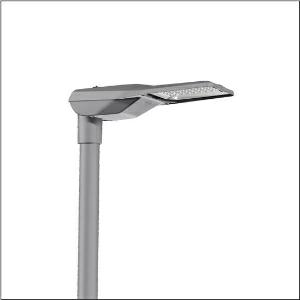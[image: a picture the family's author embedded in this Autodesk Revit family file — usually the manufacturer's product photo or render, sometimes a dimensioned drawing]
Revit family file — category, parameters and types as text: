
# Revit family: streetlight_sl_21_iq_mini___st1_0ab_5xe2m31v08jb_8772
name_source: partatom
category: Lighting Fixtures
units: mm (PartAtom-declared; Revit-internal decimal feet)

## family parameters
Cut with Voids When Loaded = No
Host = Face
Light Source = No
Part Type = Normal
Room Calculation Point = No
Round Connector Dimension = Use Diameter
Shared = No

## types (1)
- --- (1 x LED, 9870 lm, 72.5 W, 3000K)
    Apparent Load = 73 VA
    CIE Flux Codes = 40 74 97 100 100
    Color Rendering = 70
    Color Temperature = 3000K
    Default Elevation = 1800 mm
    Description = Streetlight SL 21 iQ mini, mast luminaire, primary light control with lens, of PMMA, primary optical cover: cover, of toughened safety glass, transparent, light distribution: ST1.0aB, light emission: direct distribution, primary light characteristic: asymmetric, installation type: post-top, side-entry, LED, High Power LED, rated luminous flux: 9.870lm, luminous efficacy: 136lm/W, light colour: 730, colour temperature: 3000K, control gear: iQ-Street Remote, D4i with power reduction, control: pre-setting: logarithmic dimming characteristic, Street-Remote, Auto-Match, Temp-Guard, Lumen-Switch, Night-Set, Smart-Wire, Light-Fading, Desk-Remote (wireless, voltage-free reading and setting of iQ features in the workshop via application-optimized NFC function/RFID function), optimised constant luminous flux control (CLO 2.0), mains connection: 220..240V, AC, 50/60Hz, start of lifetime: 73W, end of service life: 76W, reduction: 33W, luminaire housing, of diecast aluminium, powder-coated, SITECO metallic grey (DB 702S), corrosivity category C5 high according to DIN EN ISO 12944, please order mast flange separately, inclination adjustable: 0°, 5°, 10°, 15°, sealing non-destructively replaceable, multi-level sealing system, length: 628mm, width: 235mm, height: 110mm, mast flange for spigot size: 42mm (side-entry): 5XC10008XM4, 60/48mm (side-entry/post-top): 5XC10108XM2, 76/60mm (side-entry/post-top): 5XC10108XM1, mounting height: 4..8m, Smart Interface above, protection rating (complete): IP66, insulation class (complete): insulation class II (safety insulation), certification: CE, ENEC, ENEC+, VDE, impact resistance: IK10, permissible operating ambient temperature for outdoor applications: -40..+50°C, standard-compliant lighting for roads and squares, packaging unit: 1 piece

Light Distribution: ST1.0aB
    Height = 110 mm
    Lamp = 1 x LED
    Lamp Light Flux = 9870 lm
    Lamp Power = 72.5 W
    Lamp count = 1
    Length = 625 mm
    Luminous efficacy = 136 lm/W
    Manufacturer = Siteco
    ModVariant = No
    Model = 5XE2M31V08JB
    Mounting Place = Pole
    Mounting Type = Pole top
    Number of Poles = 1
    OnlyDefault = Yes
    Power Factor = 1
    Product Name = Streetlight SL 21 iQ mini | ST1.0aB
    Product group = mast luminaire | pylon top
    ProductGroupID = 6100
    Protection Class = Protection class II
    Protection Degree = IP 66
    RLX_Detail_Level = 1
    RLX_Emergency_Light_Flux = 0 lm
    RLX_Emergency_Type = 0
    RLX_Emergency_Type_DB = No
    RlxData = <blob elided: 92457 chars, md5=975d6f99>
    Socket = socket
    Standby Power = 0 W
    System Light Flux = 9870 lm
    System Power = 73 W
    Type Comments = factory setting: luminous flux: 100 % | dim-lin: 254 | 755 mA
    Type Image = l_1003515.jpg
    URL = http://relux.com
    VarID = @adj_113757
    Voltage = 0 V
    Weight = 0.00 kg
    Width = 234 mm

## geometry (parser evidence)
native form markers: Blend x4, Sweep x11
no freeform markers — native parametric forms only
